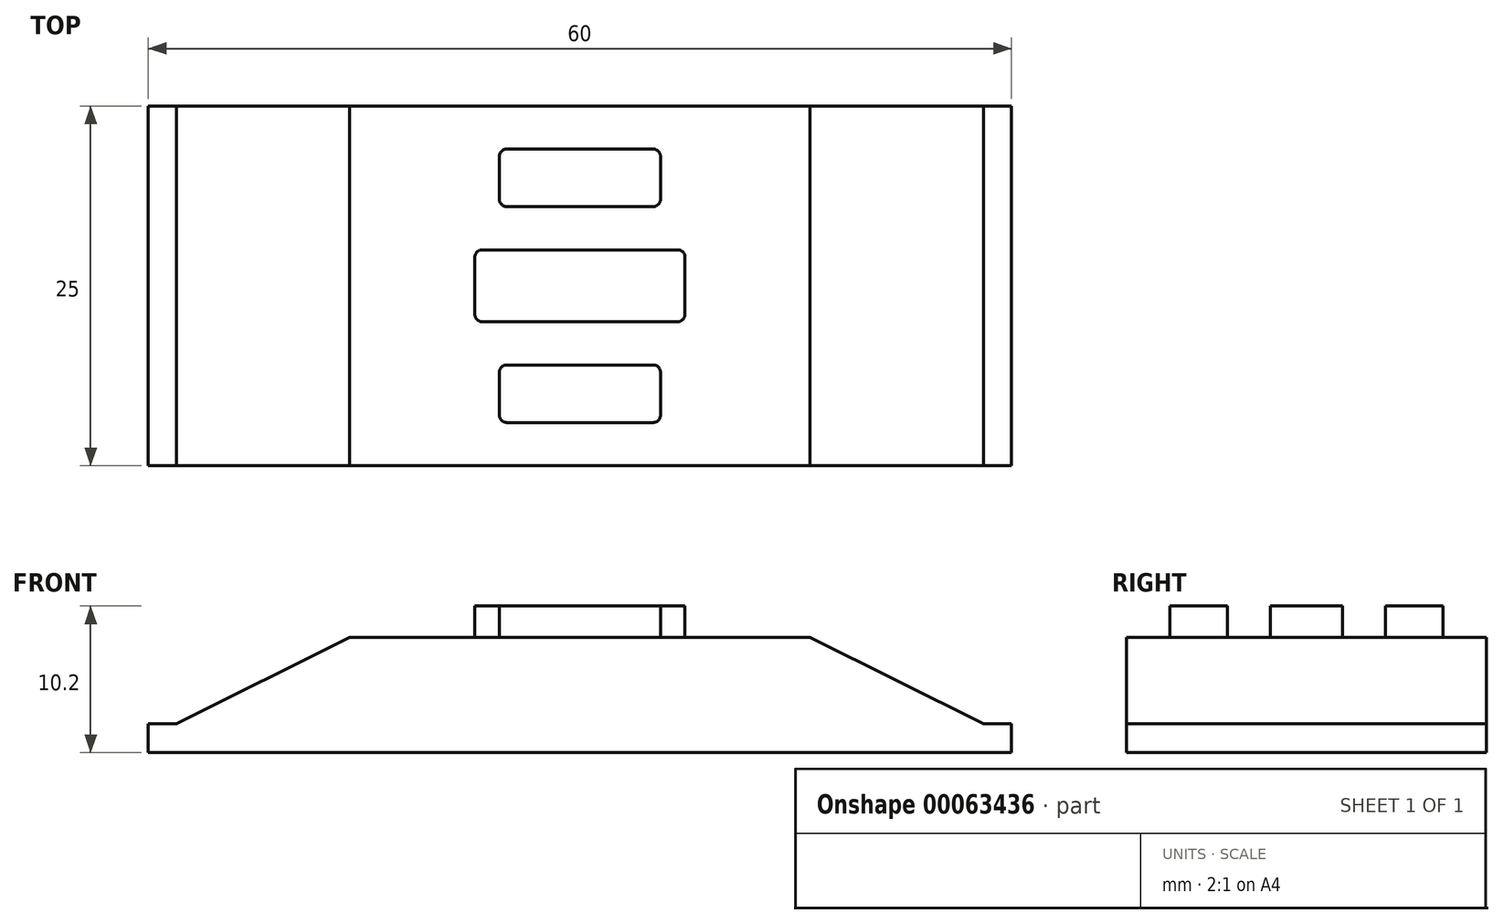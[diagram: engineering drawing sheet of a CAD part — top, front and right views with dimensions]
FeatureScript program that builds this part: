
annotation { "Feature Type Name" : "Feature", "Feature Type Description" : "" }
export const myFeature = defineFeature(function(context is Context, id is Id, definition is map)
    precondition{}
    {
        {
            var Q0;
            Q0=qCreatedBy(makeId("Top.planeOp"),FACE);
            var sketch = newSketch(context, id + "F0", { "sketchPlane" : qUnion([Q0])});
            skLineSegment(sketch, "E0.bottom", {"start": v(0, 0) * mm, "end": v(60, 0) * mm});
            skLineSegment(sketch, "E0.top", {"start": v(0, 25) * mm, "end": v(60, 25) * mm});
            skLineSegment(sketch, "E0.left", {"start": v(0, 0) * mm, "end": v(0, 25) * mm});
            skLineSegment(sketch, "E0.right", {"start": v(60, 0) * mm, "end": v(60, 25) * mm});
            skSolve(sketch);
        }
        {
            var Q0;
            Q0=makeQuery(id+"F0.imprint","IMPRINT",FACE,{"disambiguationData":[TD([[makeQuery(id+"F0.imprint","IMPRINT",EDGE,{"derivedFrom":sQuery(id+"F0.wireOp",EDGE,"E0.bottom")}),1.0]])]});
            extrude(context, id + "F1", {"entities" : qUnion([Q0]), "depth" : 2 * mm});
        }
        {
            var Q0;
            Q0=makeQuery(id+"F1.opExtrude","SWEPT_FACE",FACE,{"disambiguationData":[OSD([sQuery(id+"F0.wireOp",EDGE,"E0.top")])]});
            var sketch = newSketch(context, id + "F2", { "sketchPlane" : qUnion([Q0])});
            skLineSegment(sketch, "E1", {"start": v(-30, 0) * mm, "end": v(-30, 6.92) * mm, "construction": true});
            skLineSegment(sketch, "E2", {"start": v(-14, 8) * mm, "end": v(-1.95, 2) * mm});
            skLineSegment(sketch, "E3.MirrorCS", {"start": v(-46, 8) * mm, "end": v(-58.05, 2) * mm});
            skLineSegment(sketch, "E4", {"start": v(-1.95, 2) * mm, "end": v(-58.05, 2) * mm});
            skLineSegment(sketch, "E5", {"start": v(-46, 8) * mm, "end": v(-14, 8) * mm});
            skSolve(sketch);
        }
        {
            var Q0;
            Q0=makeQuery(id+"F2.imprint","IMPRINT",FACE,{"disambiguationData":[TD([[makeQuery(id+"F2.imprint","IMPRINT",EDGE,{"derivedFrom":sQuery(id+"F2.wireOp",EDGE,"E2")}),-1.0]])]});
            var Q1;
            Q1=makeQuery(id+"F1.opExtrude","SWEPT_FACE",FACE,{"disambiguationData":[OSD([sQuery(id+"F0.wireOp",EDGE,"E0.bottom")])]});
            extrude(context, id + "F3", {"entities" : qUnion([Q0]), "operationType" : NewBodyOperationType.ADD, "endBound" : BoundingType.UP_TO_SURFACE, "oppositeDirection" : true, "endBoundEntityFace" : qUnion([Q1]), "depth" : 25 * mm});
        }
        {
            var Q0;
            Q0=makeQuery(id+"F3.opExtrude","SWEPT_FACE",FACE,{"disambiguationData":[OSD([sQuery(id+"F2.wireOp",EDGE,"E5")])]});
            var sketch = newSketch(context, id + "F4", { "sketchPlane" : qUnion([Q0])});
            skLineSegment(sketch, "E6", {"start": v(30, 25) * mm, "end": v(30, 0) * mm, "construction": true});
            skLineSegment(sketch, "E7", {"start": v(14, 12.5) * mm, "end": v(46, 12.5) * mm, "construction": true});
            skLineSegment(sketch, "E8", {"start": v(22.7, 12) * mm, "end": v(22.7, 15) * mm});
            skLineSegment(sketch, "E9", {"start": v(22.7, 15) * mm, "end": v(37.3, 15) * mm});
            skLineSegment(sketch, "E10.MirrorCS", {"start": v(22.7, 13) * mm, "end": v(22.7, 10) * mm});
            skLineSegment(sketch, "E11.MirrorCS", {"start": v(22.7, 10) * mm, "end": v(37.3, 10) * mm});
            skLineSegment(sketch, "E12.bottom", {"start": v(24.4, 22) * mm, "end": v(35.6, 22) * mm});
            skLineSegment(sketch, "E12.top", {"start": v(24.4, 18) * mm, "end": v(35.6, 18) * mm});
            skLineSegment(sketch, "E12.left", {"start": v(24.4, 22) * mm, "end": v(24.4, 18) * mm});
            skLineSegment(sketch, "E12.right", {"start": v(35.6, 22) * mm, "end": v(35.6, 18) * mm});
            skLineSegment(sketch, "E13.MirrorCS", {"start": v(24.4, 3) * mm, "end": v(24.4, 7) * mm});
            skLineSegment(sketch, "E14.MirrorCS", {"start": v(24.4, 3) * mm, "end": v(35.6, 3) * mm});
            skLineSegment(sketch, "E15.MirrorCS", {"start": v(35.6, 3) * mm, "end": v(35.6, 7) * mm});
            skLineSegment(sketch, "E16.MirrorCS", {"start": v(24.4, 7) * mm, "end": v(35.6, 7) * mm});
            skLineSegment(sketch, "E17", {"start": v(37.3, 15) * mm, "end": v(37.3, 12.5) * mm});
            skLineSegment(sketch, "E18", {"start": v(37.3, 12.5) * mm, "end": v(37.3, 10) * mm});
            skSolve(sketch);
        }
        {
            var Q0;
            Q0=makeQuery(id+"F4.imprint","IMPRINT",FACE,{"disambiguationData":[TD([[makeQuery(id+"F4.imprint","IMPRINT",EDGE,{"derivedFrom":sQuery(id+"F4.wireOp",EDGE,"E13.MirrorCS")}),-1.0]])]});
            var Q1;
            {var subQ1=sQuery(id+"F4.wireOp",EDGE,"E9");Q1=makeQuery(id+"F4.imprint","IMPRINT",FACE,{"disambiguationData":[TD([[makeQuery(id+"F4.imprint","IMPRINT",EDGE,{"derivedFrom":subQ1}),-1.0]])]});}
            var Q2;
            Q2=makeQuery(id+"F4.imprint","IMPRINT",FACE,{"disambiguationData":[TD([[makeQuery(id+"F4.imprint","IMPRINT",EDGE,{"derivedFrom":sQuery(id+"F4.wireOp",EDGE,"E12.bottom")}),-1.0]])]});
            extrude(context, id + "F5", {"entities" : qUnion([Q0, Q1, Q2]), "operationType" : NewBodyOperationType.ADD, "depth" : 2.2 * mm});
        }
        {
            var Q0;
            Q0=makeQuery(id+"F5.opExtrude","SWEPT_EDGE",EDGE,{"disambiguationData":[OSD([sQuery(id+"F4.wireOp",EDGE,"E12.top"),sQuery(id+"F4.wireOp",EDGE,"E12.left")])]});
            var Q1;
            Q1=makeQuery(id+"F5.opExtrude","SWEPT_EDGE",EDGE,{"disambiguationData":[OSD([sQuery(id+"F4.wireOp",EDGE,"E12.top"),sQuery(id+"F4.wireOp",EDGE,"E12.right")])]});
            var Q2;
            Q2=makeQuery(id+"F5.opExtrude","SWEPT_EDGE",EDGE,{"disambiguationData":[OSD([sQuery(id+"F4.wireOp",EDGE,"1f582c0b-40f6-4354-8ecd-49a3eb3f3ee64.MirrorCS"),sQuery(id+"F4.wireOp",EDGE,"E11.MirrorCS")])]});
            var Q3;
            Q3=makeQuery(id+"F5.opExtrude","SWEPT_EDGE",EDGE,{"disambiguationData":[OSD([sQuery(id+"F4.wireOp",EDGE,"E10.MirrorCS"),sQuery(id+"F4.wireOp",EDGE,"E11.MirrorCS")])]});
            var Q4;
            Q4=makeQuery(id+"F5.opExtrude","SWEPT_EDGE",EDGE,{"disambiguationData":[OSD([sQuery(id+"F4.wireOp",EDGE,"E13.MirrorCS"),sQuery(id+"F4.wireOp",EDGE,"E14.MirrorCS")])]});
            var Q5;
            Q5=makeQuery(id+"F5.opExtrude","SWEPT_EDGE",EDGE,{"disambiguationData":[OSD([sQuery(id+"F4.wireOp",EDGE,"E14.MirrorCS"),sQuery(id+"F4.wireOp",EDGE,"E15.MirrorCS")])]});
            var Q6;
            Q6=makeQuery(id+"F5.opExtrude","SWEPT_EDGE",EDGE,{"disambiguationData":[OSD([sQuery(id+"F4.wireOp",EDGE,"E8"),sQuery(id+"F4.wireOp",EDGE,"E9")])]});
            var Q7;
            Q7=makeQuery(id+"F5.opExtrude","SWEPT_EDGE",EDGE,{"disambiguationData":[OSD([sQuery(id+"F4.wireOp",EDGE,"E9"),sQuery(id+"F4.wireOp",EDGE,"KcS1DP4q-nekC-c5Vf-fBRx-GOqZPXvvtMrM")])]});
            var Q8;
            Q8=makeQuery(id+"F5.opExtrude","SWEPT_EDGE",EDGE,{"disambiguationData":[OSD([sQuery(id+"F4.wireOp",EDGE,"E15.MirrorCS"),sQuery(id+"F4.wireOp",EDGE,"E16.MirrorCS")])]});
            var Q9;
            Q9=makeQuery(id+"F5.opExtrude","SWEPT_EDGE",EDGE,{"disambiguationData":[OSD([sQuery(id+"F4.wireOp",EDGE,"E13.MirrorCS"),sQuery(id+"F4.wireOp",EDGE,"E16.MirrorCS")])]});
            var Q10;
            Q10=makeQuery(id+"F5.opExtrude","SWEPT_EDGE",EDGE,{"disambiguationData":[OSD([sQuery(id+"F4.wireOp",EDGE,"E12.bottom"),sQuery(id+"F4.wireOp",EDGE,"E12.left")])]});
            var Q11;
            Q11=makeQuery(id+"F5.opExtrude","SWEPT_EDGE",EDGE,{"disambiguationData":[OSD([sQuery(id+"F4.wireOp",EDGE,"E12.bottom"),sQuery(id+"F4.wireOp",EDGE,"E12.right")])]});
            fillet(context, id + "F6", {"entities" : qUnion([Q0, Q1, Q2, Q3, Q4, Q5, Q6, Q7, Q8, Q9, Q10, Q11]), "radius" : 0.5 * mm, "tangentPropagation" : true, "allowEdgeOverflow" : false});
        }
    });
